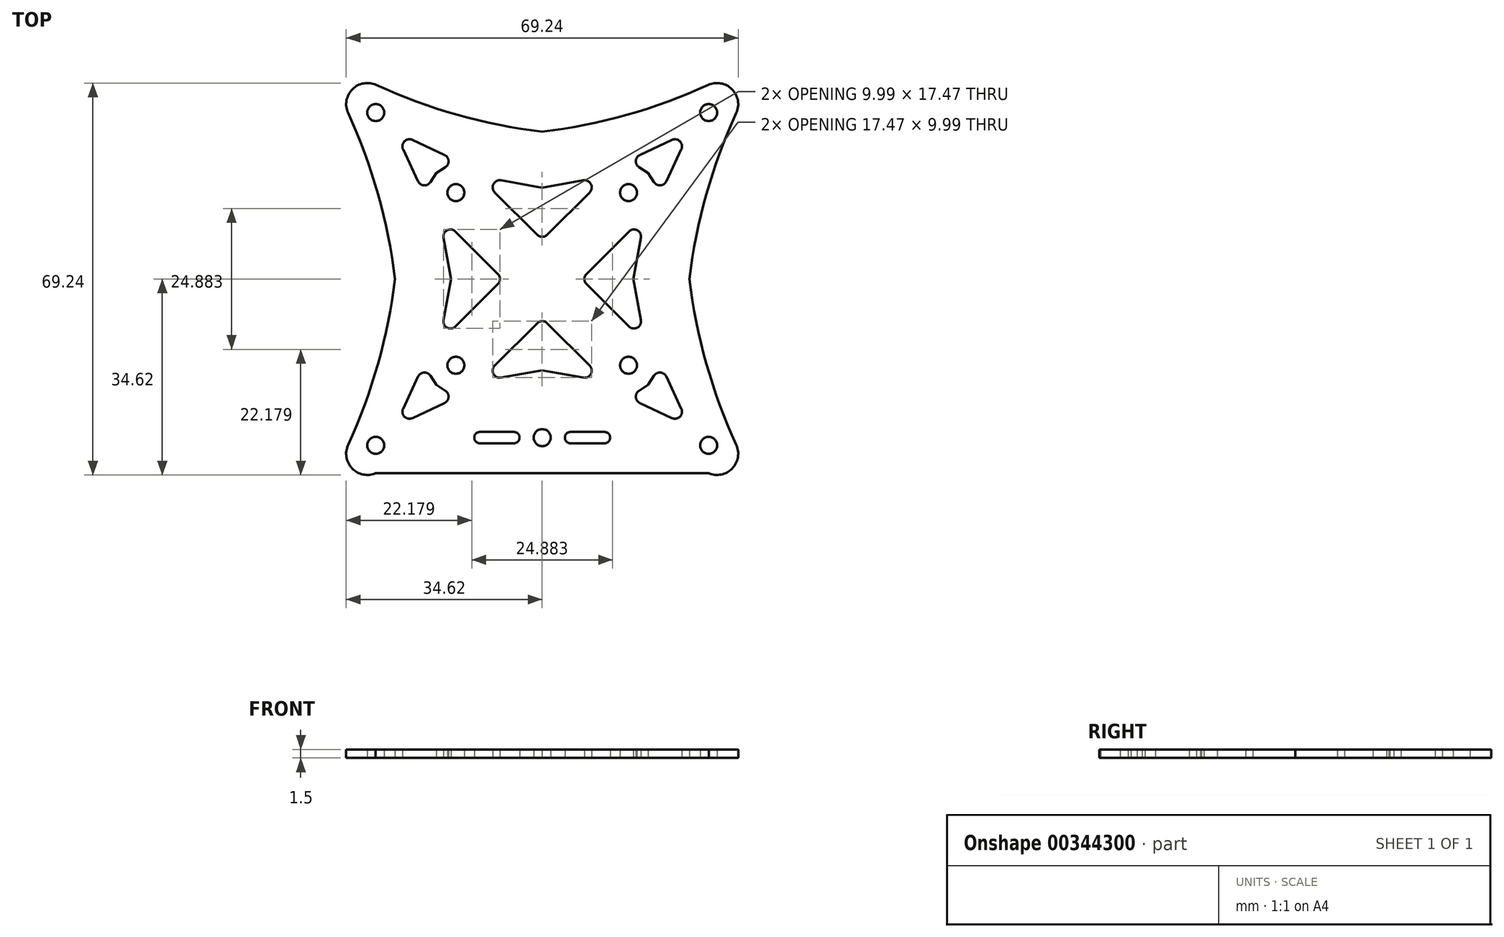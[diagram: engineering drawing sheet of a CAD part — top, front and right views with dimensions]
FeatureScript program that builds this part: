
annotation { "Feature Type Name" : "Feature", "Feature Type Description" : "" }
export const myFeature = defineFeature(function(context is Context, id is Id, definition is map)
    precondition{}
    {
        {
            var Q0;
            Q0=qCreatedBy(makeId("Top.planeOp"),FACE);
            var sketch = newSketch(context, id + "F0", { "sketchPlane" : qUnion([Q0])});
            skLineSegment(sketch, "E0", {"start": v(0, 114.28) * mm, "end": v(0, -108.92) * mm, "construction": true});
            skLineSegment(sketch, "E1", {"start": v(-111.96, 0) * mm, "end": v(120.54, 0) * mm, "construction": true});
            skLineSegment(sketch, "E2", {"start": v(0, 0) * mm, "end": v(98.63, 98.63) * mm, "construction": true});
            skLineSegment(sketch, "E3.0", {"start": v(7.81, 0.88) * mm, "end": v(15.31, 8.38) * mm});
            skCircle(sketch, "E4", {"center": v(15.25, 15.25) * mm, "radius": 1.5 * mm});
            skCircle(sketch, "E5", {"center": v(29.4, 29.4) * mm, "radius": 1.5 * mm});
            skPoint(sketch, "E6", {"position": v(33.52, 33.52) * mm});
            skArc(sketch, "E7", {"start": v(34.27, 29.3) * mm, "mid": v(34.56, 31.53) * mm, "end": v(33.52, 33.52) * mm});
            skLineSegment(sketch, "E8", {"start": v(34.47, 29.84) * mm, "end": v(26, 0) * mm, "construction": true});
            skArc(sketch, "E9", {"start": v(34.27, 29.3) * mm, "mid": v(29, 14.97) * mm, "end": v(26, 0) * mm});
            skLineSegment(sketch, "E10", {"start": v(16.13, 0) * mm, "end": v(17.43, 7.28) * mm});
            skArc(sketch, "E11", {"start": v(17.43, 7.28) * mm, "mid": v(16.78, 8.6) * mm, "end": v(15.31, 8.38) * mm});
            skLineSegment(sketch, "E12", {"start": v(18.7, 18.7) * mm, "end": v(19.74, 17.1) * mm});
            skArc(sketch, "E13", {"start": v(19.74, 17.1) * mm, "mid": v(20.87, 16.53) * mm, "end": v(21.92, 17.25) * mm});
            skArc(sketch, "E14", {"start": v(24.57, 22.9) * mm, "mid": v(24.67, 23.66) * mm, "end": v(24.32, 24.32) * mm});
            skLineSegment(sketch, "E15", {"start": v(21.92, 17.25) * mm, "end": v(24.57, 22.9) * mm});
            skArc(sketch, "E16.MirrorCS", {"start": v(29.3, 34.27) * mm, "mid": v(31.53, 34.56) * mm, "end": v(33.52, 33.52) * mm});
            skArc(sketch, "E17.MirrorCS", {"start": v(29.3, 34.27) * mm, "mid": v(14.97, 29) * mm, "end": v(0, 26) * mm});
            skArc(sketch, "E18.MirrorCS", {"start": v(22.9, 24.57) * mm, "mid": v(23.66, 24.67) * mm, "end": v(24.32, 24.32) * mm});
            skLineSegment(sketch, "E19.MirrorCS", {"start": v(17.25, 21.92) * mm, "end": v(22.9, 24.57) * mm});
            skArc(sketch, "E20.MirrorCS", {"start": v(17.1, 19.74) * mm, "mid": v(16.53, 20.87) * mm, "end": v(17.25, 21.92) * mm});
            skLineSegment(sketch, "E21.MirrorCS", {"start": v(18.7, 18.7) * mm, "end": v(17.1, 19.74) * mm});
            skLineSegment(sketch, "E22.MirrorCS", {"start": v(0, 16.13) * mm, "end": v(7.28, 17.43) * mm});
            skArc(sketch, "E23.MirrorCS", {"start": v(7.28, 17.43) * mm, "mid": v(8.6, 16.78) * mm, "end": v(8.38, 15.31) * mm});
            skLineSegment(sketch, "E24.MirrorCS", {"start": v(0.88, 7.81) * mm, "end": v(8.38, 15.31) * mm});
            skArc(sketch, "E25.MirrorCS", {"start": v(-17.1, 19.74) * mm, "mid": v(-16.53, 20.87) * mm, "end": v(-17.25, 21.92) * mm});
            skLineSegment(sketch, "E26.MirrorCS", {"start": v(-18.7, 18.7) * mm, "end": v(-19.74, 17.1) * mm});
            skArc(sketch, "E27.MirrorCS", {"start": v(-24.57, 22.9) * mm, "mid": v(-24.67, 23.66) * mm, "end": v(-24.32, 24.32) * mm});
            skArc(sketch, "E28.MirrorCS", {"start": v(-22.9, 24.57) * mm, "mid": v(-23.66, 24.67) * mm, "end": v(-24.32, 24.32) * mm});
            skLineSegment(sketch, "E29.MirrorCS", {"start": v(-18.7, 18.7) * mm, "end": v(-17.1, 19.74) * mm});
            skArc(sketch, "E30.MirrorCS", {"start": v(-19.74, 17.1) * mm, "mid": v(-20.87, 16.53) * mm, "end": v(-21.92, 17.25) * mm});
            skArc(sketch, "E31.MirrorCS", {"start": v(-7.28, 17.43) * mm, "mid": v(-8.6, 16.78) * mm, "end": v(-8.38, 15.31) * mm});
            skLineSegment(sketch, "E32.MirrorCS", {"start": v(-21.92, 17.25) * mm, "end": v(-24.57, 22.9) * mm});
            skArc(sketch, "E33.MirrorCS", {"start": v(-29.3, 34.27) * mm, "mid": v(-14.97, 29) * mm, "end": v(0, 26) * mm});
            skLineSegment(sketch, "E34.MirrorCS", {"start": v(-17.25, 21.92) * mm, "end": v(-22.9, 24.57) * mm});
            skLineSegment(sketch, "E35.MirrorCS", {"start": v(0, 16.13) * mm, "end": v(-7.28, 17.43) * mm});
            skArc(sketch, "E36.MirrorCS", {"start": v(-17.43, 7.28) * mm, "mid": v(-16.78, 8.6) * mm, "end": v(-15.31, 8.38) * mm});
            skLineSegment(sketch, "E37.MirrorCS", {"start": v(-16.13, 0) * mm, "end": v(-17.43, 7.28) * mm});
            skArc(sketch, "E38.MirrorCS", {"start": v(-34.27, 29.3) * mm, "mid": v(-29, 14.97) * mm, "end": v(-26, 0) * mm});
            skLineSegment(sketch, "E39.MirrorCS", {"start": v(-0.88, 7.81) * mm, "end": v(-8.38, 15.31) * mm});
            skArc(sketch, "E40.MirrorCS", {"start": v(-34.27, 29.3) * mm, "mid": v(-34.56, 31.53) * mm, "end": v(-33.52, 33.52) * mm});
            skArc(sketch, "E41.MirrorCS", {"start": v(-29.3, 34.27) * mm, "mid": v(-31.53, 34.56) * mm, "end": v(-33.52, 33.52) * mm});
            skCircle(sketch, "E42.MirrorC", {"center": v(-29.4, 29.4) * mm, "radius": 1.5 * mm});
            skLineSegment(sketch, "E43.MirrorCS", {"start": v(-7.81, 0.88) * mm, "end": v(-15.31, 8.38) * mm});
            skCircle(sketch, "E44.MirrorC", {"center": v(-15.25, 15.25) * mm, "radius": 1.5 * mm});
            skPoint(sketch, "E45.MirrorP", {"position": v(-33.52, 33.52) * mm});
            skArc(sketch, "E46.MirrorCS", {"start": v(24.57, -22.9) * mm, "mid": v(24.67, -23.66) * mm, "end": v(24.32, -24.32) * mm});
            skArc(sketch, "E47.MirrorCS", {"start": v(22.9, -24.57) * mm, "mid": v(23.66, -24.67) * mm, "end": v(24.32, -24.32) * mm});
            skArc(sketch, "E48.MirrorCS", {"start": v(-24.57, -22.9) * mm, "mid": v(-24.67, -23.66) * mm, "end": v(-24.32, -24.32) * mm});
            skArc(sketch, "E49.MirrorCS", {"start": v(17.1, -19.74) * mm, "mid": v(16.53, -20.87) * mm, "end": v(17.25, -21.92) * mm});
            skArc(sketch, "E50.MirrorCS", {"start": v(-17.43, -7.28) * mm, "mid": v(-16.78, -8.6) * mm, "end": v(-15.31, -8.38) * mm});
            skArc(sketch, "E51.MirrorCS", {"start": v(29.42, -34.32) * mm, "mid": v(31.6, -34.54) * mm, "end": v(33.52, -33.52) * mm});
            skArc(sketch, "E52.MirrorCS", {"start": v(34.27, -29.3) * mm, "mid": v(34.56, -31.53) * mm, "end": v(33.52, -33.52) * mm});
            skArc(sketch, "E53.MirrorCS", {"start": v(17.43, -7.28) * mm, "mid": v(16.78, -8.6) * mm, "end": v(15.31, -8.38) * mm});
            skLineSegment(sketch, "E54.MirrorCS", {"start": v(18.7, -18.7) * mm, "end": v(19.74, -17.1) * mm});
            skArc(sketch, "E55.MirrorCS", {"start": v(19.74, -17.1) * mm, "mid": v(20.87, -16.53) * mm, "end": v(21.92, -17.25) * mm});
            skArc(sketch, "E56.MirrorCS", {"start": v(-22.9, -24.57) * mm, "mid": v(-23.66, -24.67) * mm, "end": v(-24.32, -24.32) * mm});
            skArc(sketch, "E57.MirrorCS", {"start": v(-34.27, -29.3) * mm, "mid": v(-34.56, -31.53) * mm, "end": v(-33.52, -33.52) * mm});
            skArc(sketch, "E58.MirrorCS", {"start": v(7.28, -17.43) * mm, "mid": v(8.6, -16.78) * mm, "end": v(8.38, -15.31) * mm});
            skLineSegment(sketch, "E59.MirrorCS", {"start": v(18.7, -18.7) * mm, "end": v(17.1, -19.74) * mm});
            skArc(sketch, "E60.MirrorCS", {"start": v(-29.42, -34.32) * mm, "mid": v(-31.6, -34.54) * mm, "end": v(-33.52, -33.52) * mm});
            skArc(sketch, "E61.MirrorCS", {"start": v(-19.74, -17.1) * mm, "mid": v(-20.87, -16.53) * mm, "end": v(-21.92, -17.25) * mm});
            skLineSegment(sketch, "E62.MirrorCS", {"start": v(-18.7, -18.7) * mm, "end": v(-17.1, -19.74) * mm});
            skArc(sketch, "E63.MirrorCS", {"start": v(-7.28, -17.43) * mm, "mid": v(-8.6, -16.78) * mm, "end": v(-8.38, -15.31) * mm});
            skLineSegment(sketch, "E64.MirrorCS", {"start": v(-18.7, -18.7) * mm, "end": v(-19.74, -17.1) * mm});
            skArc(sketch, "E65.MirrorCS", {"start": v(-17.1, -19.74) * mm, "mid": v(-16.53, -20.87) * mm, "end": v(-17.25, -21.92) * mm});
            skLineSegment(sketch, "E66.MirrorCS", {"start": v(21.92, -17.25) * mm, "end": v(24.57, -22.9) * mm});
            skCircle(sketch, "E67.MirrorC", {"center": v(15.25, -15.25) * mm, "radius": 1.5 * mm});
            skLineSegment(sketch, "E68.MirrorCS", {"start": v(-7.81, -0.88) * mm, "end": v(-15.31, -8.38) * mm});
            skLineSegment(sketch, "E69.MirrorCS", {"start": v(7.81, -0.88) * mm, "end": v(15.31, -8.38) * mm});
            skCircle(sketch, "E70.MirrorC", {"center": v(29.4, -29.4) * mm, "radius": 1.5 * mm});
            skArc(sketch, "E71.MirrorCS", {"start": v(34.27, -29.3) * mm, "mid": v(29, -14.97) * mm, "end": v(26, 0) * mm});
            skLineSegment(sketch, "E72.MirrorCS", {"start": v(16.13, 0) * mm, "end": v(17.43, -7.28) * mm});
            skLineSegment(sketch, "E73.MirrorCS", {"start": v(17.25, -21.92) * mm, "end": v(22.9, -24.57) * mm});
            skCircle(sketch, "E74.MirrorC", {"center": v(-15.25, -15.25) * mm, "radius": 1.5 * mm});
            skLineSegment(sketch, "E75.MirrorCS", {"start": v(-17.25, -21.92) * mm, "end": v(-22.9, -24.57) * mm});
            skLineSegment(sketch, "E76.MirrorCS", {"start": v(0.88, -7.81) * mm, "end": v(8.38, -15.31) * mm});
            skLineSegment(sketch, "E77.MirrorCS", {"start": v(-0.88, -7.81) * mm, "end": v(-8.38, -15.31) * mm});
            skLineSegment(sketch, "E78.MirrorCS", {"start": v(-21.92, -17.25) * mm, "end": v(-24.57, -22.9) * mm});
            skArc(sketch, "E79.MirrorCS", {"start": v(-34.27, -29.3) * mm, "mid": v(-29, -14.97) * mm, "end": v(-26, 0) * mm});
            skLineSegment(sketch, "E80.MirrorCS", {"start": v(-16.13, 0) * mm, "end": v(-17.43, -7.28) * mm});
            skPoint(sketch, "E81.MirrorP", {"position": v(-33.52, -33.52) * mm});
            skLineSegment(sketch, "E82.MirrorCS", {"start": v(0, -16.13) * mm, "end": v(7.28, -17.43) * mm});
            skLineSegment(sketch, "E83.MirrorCS", {"start": v(0, -16.13) * mm, "end": v(-7.28, -17.43) * mm});
            skCircle(sketch, "E84.MirrorC", {"center": v(-29.4, -29.4) * mm, "radius": 1.5 * mm});
            skPoint(sketch, "E85.MirrorP", {"position": v(33.52, -33.52) * mm});
            skArc(sketch, "E86", {"start": v(7.81, 0.88) * mm, "mid": v(7.45, 0) * mm, "end": v(7.81, -0.88) * mm});
            skArc(sketch, "E87", {"start": v(-0.88, 7.81) * mm, "mid": v(0, 7.45) * mm, "end": v(0.88, 7.81) * mm});
            skArc(sketch, "E88", {"start": v(-7.81, -0.88) * mm, "mid": v(-7.45, 0) * mm, "end": v(-7.81, 0.88) * mm});
            skArc(sketch, "E89", {"start": v(0.88, -7.81) * mm, "mid": v(0, -7.45) * mm, "end": v(-0.88, -7.81) * mm});
            skPoint(sketch, "E90.orphan", {"position": v(6.93, 0) * mm});
            skPoint(sketch, "E91.orphan", {"position": v(0, -6.93) * mm});
            skPoint(sketch, "E92.orphan", {"position": v(-6.93, 0) * mm});
            skPoint(sketch, "E93.orphan", {"position": v(0, 6.93) * mm});
            skLineSegment(sketch, "E94", {"start": v(-29.42, -34.33) * mm, "end": v(29.42, -34.33) * mm});
            skCircle(sketch, "E95", {"center": v(0, -28.03) * mm, "radius": 1.5 * mm});
            skArc(sketch, "E96", {"start": v(5, -27.03) * mm, "mid": v(4, -28.03) * mm, "end": v(5, -29.03) * mm});
            skArc(sketch, "E97", {"start": v(11, -29.03) * mm, "mid": v(12, -28.03) * mm, "end": v(11, -27.03) * mm});
            skLineSegment(sketch, "E98", {"start": v(11, -27.03) * mm, "end": v(5, -27.03) * mm});
            skLineSegment(sketch, "E99", {"start": v(11, -29.03) * mm, "end": v(5, -29.03) * mm});
            skArc(sketch, "E100.MirrorCS", {"start": v(-5, -27.03) * mm, "mid": v(-4, -28.03) * mm, "end": v(-5, -29.03) * mm});
            skLineSegment(sketch, "E101.MirrorCS", {"start": v(-11, -29.03) * mm, "end": v(-5, -29.03) * mm});
            skLineSegment(sketch, "E102.MirrorCS", {"start": v(-11, -27.03) * mm, "end": v(-5, -27.03) * mm});
            skArc(sketch, "E103.MirrorCS", {"start": v(-11, -29.03) * mm, "mid": v(-12, -28.03) * mm, "end": v(-11, -27.03) * mm});
            skSolve(sketch);
        }
        {
            var Q0;
            Q0=makeQuery(id+"F0.imprint","IMPRINT",FACE,{"disambiguationData":[TD([[makeQuery(id+"F0.imprint","IMPRINT",EDGE,{"derivedFrom":sQuery(id+"F0.wireOp",EDGE,"E3.0")}),1.0]])]});
            extrude(context, id + "F1", {"entities" : qUnion([Q0]), "depth" : 1.5 * mm});
        }
    });
